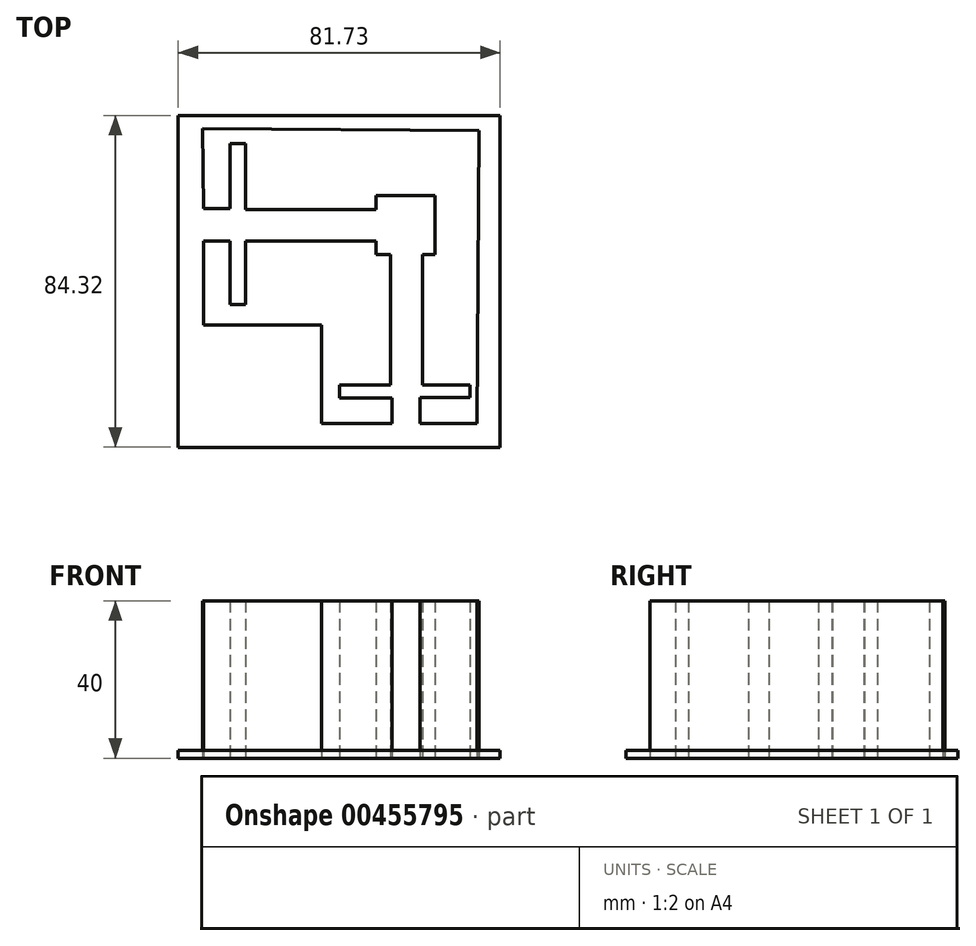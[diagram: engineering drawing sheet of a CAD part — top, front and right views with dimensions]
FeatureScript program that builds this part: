
annotation { "Feature Type Name" : "Feature", "Feature Type Description" : "" }
export const myFeature = defineFeature(function(context is Context, id is Id, definition is map)
    precondition{}
    {
        {
            var Q0;
            Q0=qCreatedBy(makeId("Top.planeOp"),FACE);
            var sketch = newSketch(context, id + "F0", { "sketchPlane" : qUnion([Q0])});
            skLineSegment(sketch, "E0.left", {"start": v(-40, 0) * mm, "end": v(-40, -25) * mm});
            skLineSegment(sketch, "E1.bottom", {"start": v(-26.2, 32.84) * mm, "end": v(-11.2, 32.84) * mm});
            skLineSegment(sketch, "E1.right", {"start": v(-11.2, 32.84) * mm, "end": v(-11.2, 17.84) * mm});
            skLineSegment(sketch, "E2.top", {"start": v(-26.2, 21.3) * mm, "end": v(-59.29, 21.3) * mm});
            skLineSegment(sketch, "E3.bottom", {"start": v(-59.29, 46.05) * mm, "end": v(-63.32, 46.05) * mm});
            skLineSegment(sketch, "E3.top", {"start": v(-59.29, 5.18) * mm, "end": v(-63.32, 5.18) * mm});
            skLineSegment(sketch, "E4.left", {"start": v(-22.45, 17.84) * mm, "end": v(-22.45, -15.25) * mm});
            skLineSegment(sketch, "E5", {"start": v(-26.2, 17.84) * mm, "end": v(-22.45, 17.84) * mm});
            skLineSegment(sketch, "E6", {"start": v(-14.4, 17.84) * mm, "end": v(-11.2, 17.84) * mm});
            skLineSegment(sketch, "E7", {"start": v(-26.2, 32.84) * mm, "end": v(-26.2, 29.36) * mm});
            skLineSegment(sketch, "E8", {"start": v(-26.2, 21.3) * mm, "end": v(-26.2, 17.84) * mm});
            skLineSegment(sketch, "E9", {"start": v(-59.29, 46.05) * mm, "end": v(-59.29, 29.36) * mm});
            skLineSegment(sketch, "E10", {"start": v(-59.29, 21.3) * mm, "end": v(-59.29, 5.18) * mm});
            skLineSegment(sketch, "E11", {"start": v(-35.49, -15.25) * mm, "end": v(-22.45, -15.25) * mm});
            skLineSegment(sketch, "E12", {"start": v(-14.4, -15.25) * mm, "end": v(-1.6, -15.25) * mm});
            skLineSegment(sketch, "E13.left", {"start": v(-35.49, -15.25) * mm, "end": v(-35.49, -18.51) * mm});
            skLineSegment(sketch, "E13.right", {"start": v(-2.37, -15.24) * mm, "end": v(-2.37, -18.5) * mm});
            skLineSegment(sketch, "E14.left", {"start": v(-22.12, -18.51) * mm, "end": v(-22.12, -25) * mm});
            skLineSegment(sketch, "E14.right", {"start": v(-15.02, -18.5) * mm, "end": v(-15.02, -25) * mm});
            skLineSegment(sketch, "E15.bottom", {"start": v(-63.32, 29.56) * mm, "end": v(-70, 29.56) * mm});
            skLineSegment(sketch, "E15.top", {"start": v(-63.32, 21.33) * mm, "end": v(-70, 21.33) * mm});
            skLineSegment(sketch, "E16", {"start": v(-63.32, 46.05) * mm, "end": v(-63.32, 29.56) * mm});
            skLineSegment(sketch, "E17", {"start": v(-63.32, 21.33) * mm, "end": v(-63.32, 5.18) * mm});
            skLineSegment(sketch, "E18", {"start": v(-35.49, -18.51) * mm, "end": v(-22.12, -18.51) * mm});
            skLineSegment(sketch, "E19", {"start": v(-15.02, -18.5) * mm, "end": v(-2.37, -18.5) * mm});
            skLineSegment(sketch, "E20", {"start": v(-40, -25) * mm, "end": v(-22.12, -25) * mm});
            skLineSegment(sketch, "E21", {"start": v(-15.02, -25) * mm, "end": v(-0.51, -25) * mm});
            skLineSegment(sketch, "E22", {"start": v(-70, 0) * mm, "end": v(-40, 0) * mm});
            skLineSegment(sketch, "E23", {"start": v(-70.28, 49.89) * mm, "end": v(-70, 29.56) * mm});
            skLineSegment(sketch, "E24", {"start": v(-70, 21.33) * mm, "end": v(-70, 0) * mm});
            skLineSegment(sketch, "E25", {"start": v(0, 49.4) * mm, "end": v(-0.51, -25) * mm});
            skLineSegment(sketch, "E26", {"start": v(-70.28, 49.89) * mm, "end": v(0, 49.4) * mm});
            skLineSegment(sketch, "E27", {"start": v(-14.4, 17.84) * mm, "end": v(-14.4, -15.25) * mm});
            skLineSegment(sketch, "E28", {"start": v(-26.2, 29.36) * mm, "end": v(-59.29, 29.36) * mm});
            skSolve(sketch);
        }
        {
            var Q0;
            Q0=makeQuery(id+"F0.imprint","IMPRINT",FACE,{"disambiguationData":[TD([[makeQuery(id+"F0.imprint","IMPRINT",EDGE,{"derivedFrom":sQuery(id+"F0.wireOp",EDGE,"E0.left")}),1.0]])]});
            var Q1;
            Q1=makeQuery(id+"F0.imprint","IMPRINT",FACE,{"disambiguationData":[TD([[makeQuery(id+"F0.imprint","IMPRINT",EDGE,{"derivedFrom":sQuery(id+"F0.wireOp",EDGE,"E1.bottom")}),1.0]])]});
            extrude(context, id + "F1", {"entities" : qUnion([Q0, Q1]), "depth" : 40 * mm});
        }
        {
            var Q0;
            Q0=qCreatedBy(makeId("Top.planeOp"),FACE);
            var sketch = newSketch(context, id + "F2", { "sketchPlane" : qUnion([Q0])});
            skLineSegment(sketch, "E29.bottom", {"start": v(-76.41, -31.08) * mm, "end": v(5.32, -31.08) * mm});
            skLineSegment(sketch, "E29.top", {"start": v(-76.41, 53.24) * mm, "end": v(5.32, 53.24) * mm});
            skLineSegment(sketch, "E29.left", {"start": v(-76.41, -31.08) * mm, "end": v(-76.41, 53.24) * mm});
            skLineSegment(sketch, "E29.right", {"start": v(5.32, -31.08) * mm, "end": v(5.32, 53.24) * mm});
            skSolve(sketch);
        }
        {
            var Q0;
            Q0=makeQuery(id+"F2.imprint","IMPRINT",FACE,{"disambiguationData":[TD([[makeQuery(id+"F2.imprint","IMPRINT",EDGE,{"derivedFrom":sQuery(id+"F2.wireOp",EDGE,"E29.bottom")}),1.0]])]});
            extrude(context, id + "F3", {"entities" : qUnion([Q0]), "depth" : 2 * mm});
        }
    });
